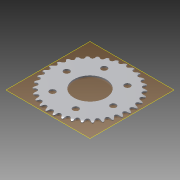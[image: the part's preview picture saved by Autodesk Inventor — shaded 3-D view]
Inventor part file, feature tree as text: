
AUTODESK INVENTOR PART (.ipt)
format: ipt  version: 2013 (Build 170138000, 138)  size: 884,224 bytes
history: native  units: mm
features: other x6, extrude x2, hole x2, sketch x2, pattern_linear x1, pattern_circular x1, plane x1
ambient origin geometry x8: Origin, YZ Plane, XZ Plane, XY Plane, X Axis, Y Axis, Z Axis, Center Point
bodies: Solid1 (feature_tree)
feature tree (15):
  other  "Theoretical Tooth Profile"
  other  "Tooth Profile"
  other  "Section Profile"
  other  "Shroud"
  other  "Strand"
  pattern_linear  "Strand Pattern"  Spacing1=1.697355mm  [1 undecoded]
  extrude  "Theoretical Tooth"  Depth=22.124615mm
  extrude  "Tooth"  Depth=2.854127mm
  pattern_circular  "Tooth Pattern"  [2 undecoded]
  other  "Timing Plane"
  hole  "Hole1"  [1 undecoded]
  hole  "Hole2"  [1 undecoded]
  plane  "Work Plane3"
  sketch  "Sketch4"  dims[d0=68.820992mm]
  sketch  "Sketch5"  dims[d2=1.847996mm d3=1.697355mm d10=22.124615mm d11=2.854127mm d12=2.6416mm d13=4.338955mm d14=4.6228mm d18=10.0mm d19=0.0mm d20=340.0mm d21=360.0deg d23=1.905mm d28=0.0mm d29=0.0mm d30=2.286mm d31=56.852632mm d32=2.286mm d33=0.79375mm d34=6.75005mm d36=90.0deg d37=90.0deg d38=10.0mm d40=6.4008mm d42=0.0mm d43=1.143mm d44=23.943736mm d45=1.697355mm d46=13.47216mm d47=0.0mm d48=25.4mm d49=0.0mm d50=10.0mm d51=28.5623mm d52=19.05mm d53=9.525mm d54=6.35mm d55=14.3117mm d56=25.4mm d57=20.594885mm d58=47.625mm d59=60.0mm d61=360.0deg d63=5.2324mm d64=19.05mm d65=9.525mm d66=6.35mm d67=14.3117mm d68=25.4mm d69=20.594885mm d70=0.0mm]
note: 5 required parameter values undecoded (feature->parameter linkage not recoverable at this tier; creation-order binding heuristic only, values carry confidence <= 0.55)
